# Revit family: xsolar_l-s_009823
name_source: partatom
category: Leuchten
revit_build: Autodesk Revit 2016 (Build: 20190508_0715(x64)
units: mm (PartAtom-declared; Revit-internal decimal feet)

## family parameters
Basisbauteil = Fläche
Beim Laden mit Abzugskörper schneiden = Nein
Bemaßung runder Anschluss = Durchmesser verwenden
Gemeinsam genutzt = Nein
Lichtquelle = Nein
Raumberechnungspunkt = Nein
Teiletyp = Normal

## types (1)
- XSolar L-S (1 x , 150 lm, 4000 K)
    Beschreibung = Dimensions (L x W x H): 187 x 189 x 298 mm; Sensor Technology: passive infrared; Output: 1,2 W; Luminous flux: 150 lm; Colour temperature: 4000 K; Colour variation LED: SDCM5; Colour Rendering Index CRI: 80-89; With lamp: Yes, STEINEL LED system; Lamp: LED cannot be replaced; LED life expectancy (max. °C): 50000 h; Drop in luminous flux in accordance with LM80: L70B10; LED cooling system: Passive Thermo Control; Detection angle: 140 °; Sneak-by guard: Yes; Reach, radial: r = 2 m (5 m²); Reach, tangential: r = 8 m (78 m²); Photo-cell controller: Yes; Twilight setting: 2 lx; Time setting: 10 sec – 1 min; Basic light level function: Yes; Basic light level function time: all night; Functions: Motions sensor; Soft light start: No; Impact resistance: IK03; IP-rating: IP44; Protection class: III; Ambient temperature: -20 – 40 °C; Housing material: Plastic; Cover material: Plastic, transparent; Manufacturer's Warranty: 5 years; Included extension cable: 6 m; Version: Anthracite; PU1, EAN: 4007841009823
    Color Rendering = 80-89
    Color Temperature = 4000 K
    Height = 298 mm
    Hersteller = Steinel
    Lamp Light Flux = 150 lm
    Lamp count = 1
    Lampe = 1 x
    Length = 187 mm
    Luminous efficacy = 0 lm/W
    ModVariant = Nein
    Modell = 009823
    Mounting Type = Surface mounted
    Number of Poles = 1
    OnlyDefault = Ja
    Power Factor = 1
    Product Name = XSolar L-S
    Product group = Sensor-switched indoor light
    ProductGroupID = 30
    Protection Class = Safety extra-low voltage
    Protection Degree = IP 34
    RlxData = <blob elided: 28901 chars, md5=9293c921>
    Scheinlast = 1 VA
    Socket = socket
    Standby Power = 0 W
    System Light Flux = 0 lm
    System Power = 1 W
    Typenbild = produkt1_009823.jpg
    Typenkommentare = Product without accessories
    URL = http://relux.com
    VarID = ---
    Voltage = 0 V
    Vorgabe-Ansicht = 1800 mm
    Weight = 0.00 kg
    Width = 189 mm

## geometry (parser evidence)
native form markers: Blend x4, Sweep x9
no freeform markers — native parametric forms only
